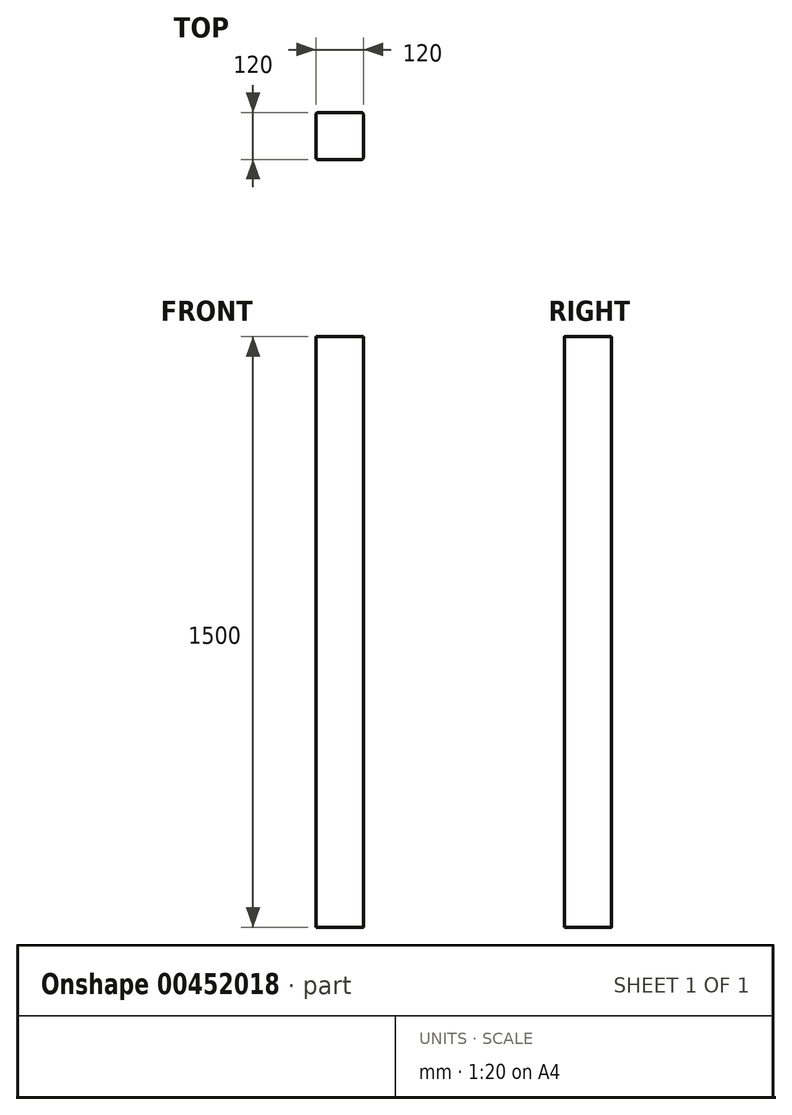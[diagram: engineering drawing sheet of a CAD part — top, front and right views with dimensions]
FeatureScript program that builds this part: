
annotation { "Feature Type Name" : "Feature", "Feature Type Description" : "" }
export const myFeature = defineFeature(function(context is Context, id is Id, definition is map)
    precondition{}
    {
        {
            var Q0;
            Q0=qCreatedBy(makeId("Top.planeOp"),FACE);
            var sketch = newSketch(context, id + "F0", { "sketchPlane" : qUnion([Q0])});
            skLineSegment(sketch, "E0.bottom", {"start": v(55, 60) * mm, "end": v(-55, 60) * mm});
            skLineSegment(sketch, "E0.top", {"start": v(55, -60) * mm, "end": v(-55, -60) * mm});
            skLineSegment(sketch, "E0.left", {"start": v(60, 55) * mm, "end": v(60, -55) * mm});
            skLineSegment(sketch, "E0.right", {"start": v(-60, 55) * mm, "end": v(-60, -55) * mm});
            skPoint(sketch, "E0.middle", {"position": v(0, 0) * mm});
            skPoint(sketch, "E1.visualSharp", {"position": v(-60, 60) * mm});
            skArc(sketch, "E1.filletArc", {"start": v(-55, 60) * mm, "mid": v(-58.54, 58.54) * mm, "end": v(-60, 55) * mm});
            skPoint(sketch, "E2.visualSharp", {"position": v(60, 60) * mm});
            skArc(sketch, "E2.filletArc", {"start": v(60, 55) * mm, "mid": v(58.54, 58.54) * mm, "end": v(55, 60) * mm});
            skPoint(sketch, "E3.visualSharp", {"position": v(60, -60) * mm});
            skArc(sketch, "E3.filletArc", {"start": v(55, -60) * mm, "mid": v(58.54, -58.54) * mm, "end": v(60, -55) * mm});
            skPoint(sketch, "E4.visualSharp", {"position": v(-60, -60) * mm});
            skArc(sketch, "E4.filletArc", {"start": v(-60, -55) * mm, "mid": v(-58.54, -58.54) * mm, "end": v(-55, -60) * mm});
            skSolve(sketch);
        }
        {
            var Q0;
            Q0 = qSketchRegion(id + "F0", true);
            extrude(context, id + "F1", {"entities" : qUnion([Q0]), "depth" : 1500 * mm, "offsetDistance" : 25 * mm});
        }
    });
